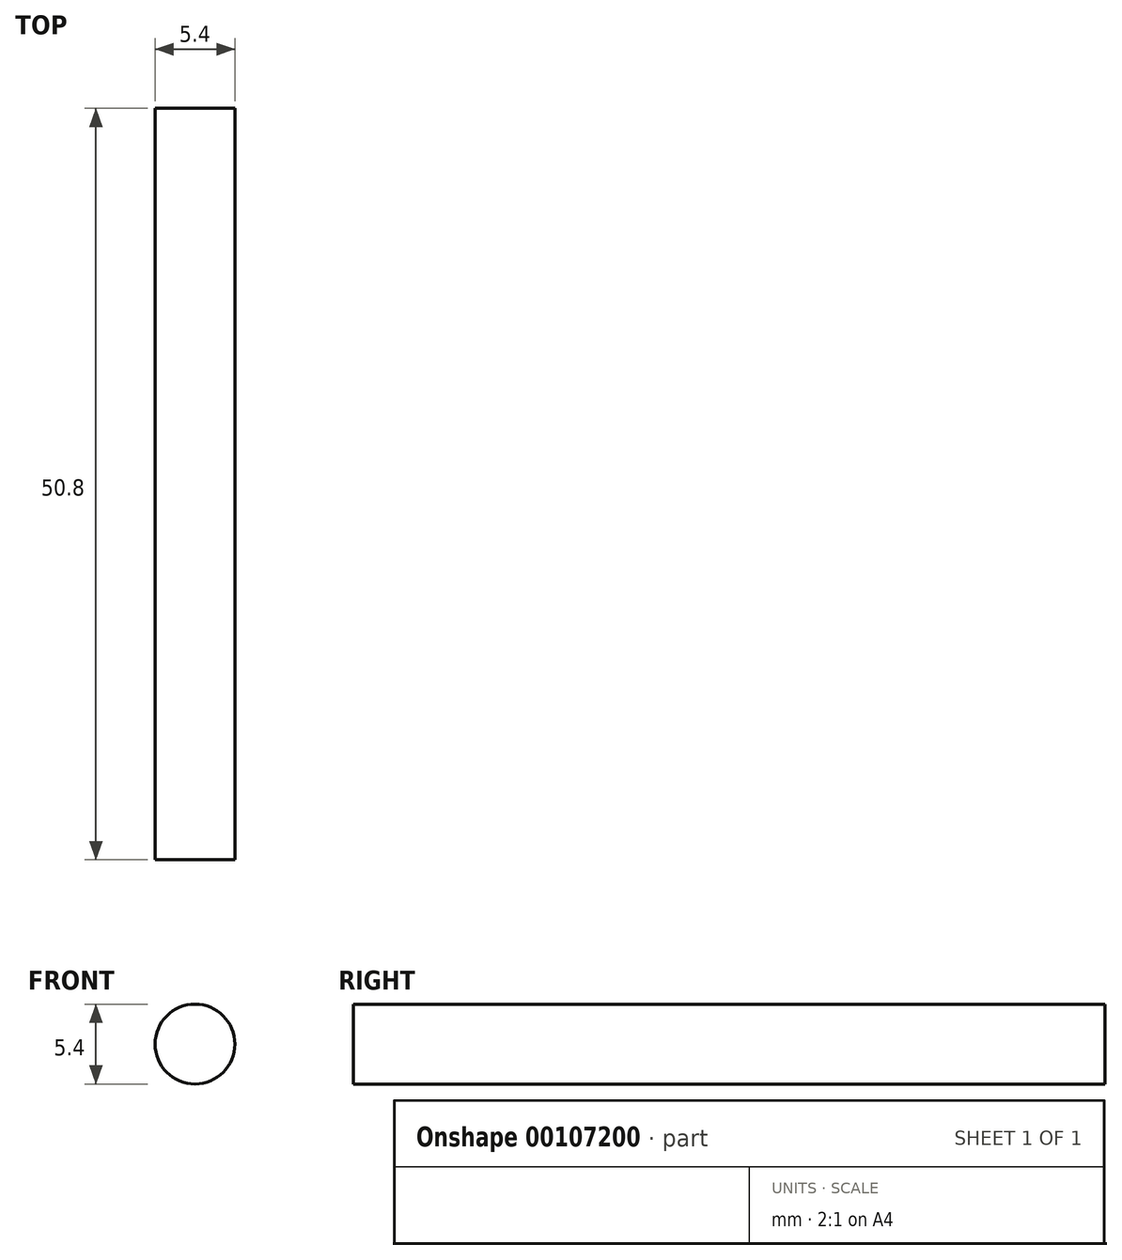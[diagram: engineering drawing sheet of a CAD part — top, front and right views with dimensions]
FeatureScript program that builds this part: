
annotation { "Feature Type Name" : "Feature", "Feature Type Description" : "" }
export const myFeature = defineFeature(function(context is Context, id is Id, definition is map)
    precondition{}
    {
        {
            var Q0;
            Q0=qCreatedBy(makeId("Front.planeOp"),FACE);
            var sketch = newSketch(context, id + "F0", { "sketchPlane" : qUnion([Q0])});
            skPoint(sketch, "E0", {"position": v(-71.34, 27.66) * mm});
            skCircle(sketch, "E1", {"center": v(-71.34, 27.66) * mm, "radius": 2.7 * mm});
            skSolve(sketch);
        }
        {
            var Q0;
            Q0=makeQuery(id+"F0.imprint","IMPRINT",FACE,{"disambiguationData":[TD([[makeQuery(id+"F0.imprint","IMPRINT",EDGE,{"derivedFrom":sQuery(id+"F0.wireOp",EDGE,"E1")}),1.0]])]});
            extrude(context, id + "F1", {"entities" : qUnion([Q0]), "depth" : 50.8 * mm});
        }
    });
